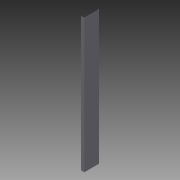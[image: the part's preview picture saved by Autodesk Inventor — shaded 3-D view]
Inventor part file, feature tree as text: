
AUTODESK INVENTOR PART (.ipt)
format: ipt  version: 2014 (Build 180170000, 170)  size: 126,976 bytes
history: native  units: in
note: dims shown in document units (in); Inventor stores cm internally (conversion verified against a paired STEP export)
features: sketch x2, extrude x1, hole x1, pattern_linear x1
ambient origin geometry x8: Origin, YZ Plane, XZ Plane, XY Plane, X Axis, Y Axis, Z Axis, Center Point
bodies: Solid1 (feature_tree)
feature tree (5):
  extrude  "Extrusion1"  Depth=0.75in
  hole  "Hole1"  [1 undecoded]
  pattern_linear  "Rectangular Pattern1"  Spacing1=32.0in  [1 undecoded]
  sketch  "Sketch1"  dims[d0=3.5in d1=0.75in]
  sketch  "Sketch2"  dims[d2=0.025in d4=0.025in d5=32.0in d6=0.0in d7=0.25in d8=0.5in d9=0.1in d10=0.75in d11=0.375in d12=0.25in d13=0.5635in d14=0.12in d15=0.8108in d16=12.5984in d18=1.0in]
note: 2 required parameter values undecoded (feature->parameter linkage not recoverable at this tier; creation-order binding heuristic only, values carry confidence <= 0.55)
